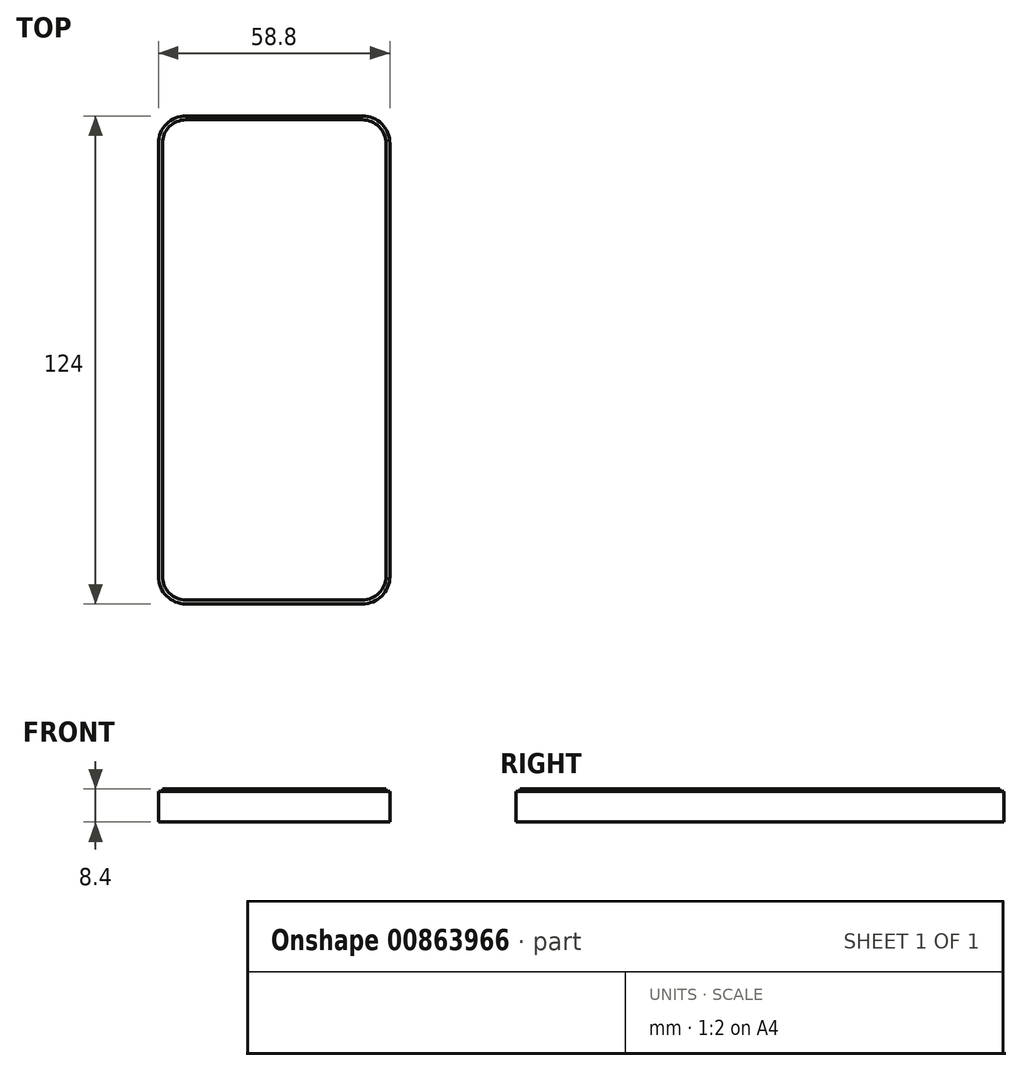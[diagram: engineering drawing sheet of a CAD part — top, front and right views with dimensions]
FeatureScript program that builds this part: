
annotation { "Feature Type Name" : "Feature", "Feature Type Description" : "" }
export const myFeature = defineFeature(function(context is Context, id is Id, definition is map)
    precondition{}
    {
        {
            var Q0;
            Q0=qCreatedBy(makeId("Top.planeOp"),FACE);
            var sketch = newSketch(context, id + "F0", { "sketchPlane" : qUnion([Q0])});
            skLineSegment(sketch, "E0.bottom", {"start": v(-22.4, 62) * mm, "end": v(22.4, 62) * mm});
            skLineSegment(sketch, "E0.top", {"start": v(-22.4, -62) * mm, "end": v(22.4, -62) * mm});
            skLineSegment(sketch, "E0.left", {"start": v(-29.4, 55) * mm, "end": v(-29.4, -55) * mm});
            skLineSegment(sketch, "E0.right", {"start": v(29.4, 55) * mm, "end": v(29.4, -55) * mm});
            skLineSegment(sketch, "E1", {"start": v(0, -62) * mm, "end": v(0, 0) * mm, "construction": true});
            skLineSegment(sketch, "E2", {"start": v(0, 0) * mm, "end": v(29.4, 0) * mm, "construction": true});
            skPoint(sketch, "E3.visualSharp", {"position": v(-29.4, 62) * mm});
            skArc(sketch, "E3.filletArc", {"start": v(-22.4, 62) * mm, "mid": v(-27.35, 59.95) * mm, "end": v(-29.4, 55) * mm});
            skPoint(sketch, "E4.visualSharp", {"position": v(29.4, 62) * mm});
            skArc(sketch, "E4.filletArc", {"start": v(29.4, 55) * mm, "mid": v(27.35, 59.95) * mm, "end": v(22.4, 62) * mm});
            skPoint(sketch, "E5.visualSharp", {"position": v(-29.4, -62) * mm});
            skArc(sketch, "E5.filletArc", {"start": v(-29.4, -55) * mm, "mid": v(-27.35, -59.95) * mm, "end": v(-22.4, -62) * mm});
            skPoint(sketch, "E6.visualSharp", {"position": v(29.4, -62) * mm});
            skArc(sketch, "E6.filletArc", {"start": v(22.4, -62) * mm, "mid": v(27.35, -59.95) * mm, "end": v(29.4, -55) * mm});
            skLineSegment(sketch, "E7.0", {"start": v(-22.4, 61) * mm, "end": v(22.4, 61) * mm});
            skArc(sketch, "E7.1", {"start": v(28.4, 55) * mm, "mid": v(26.64, 59.24) * mm, "end": v(22.4, 61) * mm});
            skArc(sketch, "E7.2", {"start": v(-22.4, 61) * mm, "mid": v(-26.64, 59.24) * mm, "end": v(-28.4, 55) * mm});
            skLineSegment(sketch, "E7.3", {"start": v(28.4, 55) * mm, "end": v(28.4, -55) * mm});
            skLineSegment(sketch, "E7.4", {"start": v(-28.4, 55) * mm, "end": v(-28.4, -55) * mm});
            skArc(sketch, "E7.5", {"start": v(-28.4, -55) * mm, "mid": v(-26.64, -59.24) * mm, "end": v(-22.4, -61) * mm});
            skLineSegment(sketch, "E7.6", {"start": v(-22.4, -61) * mm, "end": v(22.4, -61) * mm});
            skArc(sketch, "E7.7", {"start": v(22.4, -61) * mm, "mid": v(26.64, -59.24) * mm, "end": v(28.4, -55) * mm});
            skSolve(sketch);
        }
        {
            var Q0;
            Q0=makeQuery(id+"F0.imprint","IMPRINT",FACE,{"disambiguationData":[TD([[makeQuery(id+"F0.imprint","IMPRINT",EDGE,{"derivedFrom":sQuery(id+"F0.wireOp",EDGE,"E7.0")}),-1.0]])]});
            extrude(context, id + "F1", {"entities" : qUnion([Q0]), "depth" : 8.4 * mm, "offsetDistance" : 25 * mm});
        }
        {
            var Q0;
            Q0=makeQuery(id+"F0.imprint","IMPRINT",FACE,{"disambiguationData":[TD([[makeQuery(id+"F0.imprint","IMPRINT",EDGE,{"derivedFrom":sQuery(id+"F0.wireOp",EDGE,"E0.bottom")}),-1.0]])]});
            extrude(context, id + "F2", {"entities" : qUnion([Q0]), "operationType" : NewBodyOperationType.ADD, "depth" : 7.8 * mm, "offsetDistance" : 25 * mm});
        }
    });
